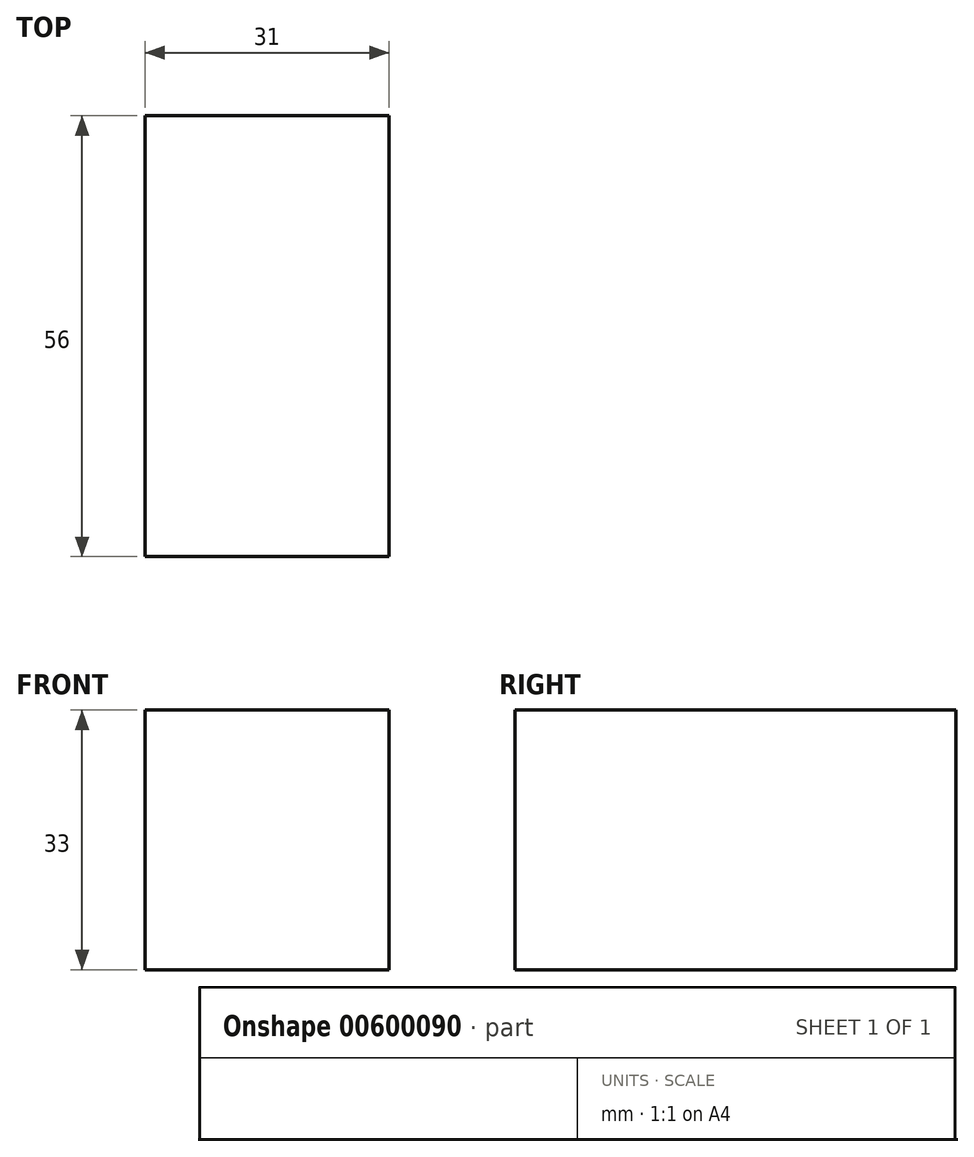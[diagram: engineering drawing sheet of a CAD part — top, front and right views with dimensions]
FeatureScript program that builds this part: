
annotation { "Feature Type Name" : "Feature", "Feature Type Description" : "" }
export const myFeature = defineFeature(function(context is Context, id is Id, definition is map)
    precondition{}
    {
        {
            var Q0;
            Q0=qCreatedBy(makeId("Top.planeOp"),FACE);
            var sketch = newSketch(context, id + "F0", { "sketchPlane" : qUnion([Q0])});
            skLineSegment(sketch, "E0.bottom", {"start": v(15.5, -28) * mm, "end": v(-15.5, -28) * mm});
            skLineSegment(sketch, "E0.top", {"start": v(15.5, 28) * mm, "end": v(-15.5, 28) * mm});
            skLineSegment(sketch, "E0.left", {"start": v(15.5, -28) * mm, "end": v(15.5, 28) * mm});
            skLineSegment(sketch, "E0.right", {"start": v(-15.5, -28) * mm, "end": v(-15.5, 28) * mm});
            skPoint(sketch, "E0.middle", {"position": v(0, 0) * mm});
            skSolve(sketch);
        }
        {
            var Q0;
            Q0=qSketchRegion(id+"F0",true);
            extrude(context, id + "F1", {"entities" : qUnion([Q0]), "depth" : 33 * mm});
        }
    });
